# Revit family: Холодильные шкафы со стеклянными дверьми POLAIR Grande
name_source: partatom
category: Оборудование
units: mm (PartAtom-declared; Revit-internal decimal feet)

## family parameters
Всегда вертикально = Да
Классификация = Нет
На основе рабочей плоскости = Нет
Общий = Нет
При загрузке вырезать с полостями = Нет
Размер круглого соединителя = Использовать диаметр
Тип детали = Нормальный
Точка расчета площади = Нет

## types (2) — shared parameters
Высота = 1960 мм
Диап. рабочих температур = +1....+10
Допустимая нагрузка на полку, кг = 40
Замок = опция
Канапе с подсветкой = LED
Клапан Шредера = +
Кол-во полок = 4
Подсветка = LED вертикальная
Размеры в упаковке, мм = 790х744х2125
Расположение агрегата = верхнее
Система электропитания В/Гц = 230/50
Терморегулятор = эл.  блок
Тип оттайки = автомат. с системой исп. конденсата
Тип охлаждения = динамический
Условия окр. среды (темп./вл-сть,%) = до +32/до 60
Хладагент = R134a
Холодильный шкаф = <По категории>
Ширина = 697 мм
zero-valued in all types: Отметка по умолчанию

## per-type parameters (varying)
| type | Вес брутто, кг | Вес нетто, кг | Габаритные размеры, мм | Глубина | Кол-во бутылок 0,5 л по глубине 1 полки, шт. | Кол-во бутылок 0,5 по ширине 1 полки, шт. | Объем, л. | Потребляемая мощность, Вт, не более | Размер полки, мм | Расход электроэнергии за сутки, кВт/ч | Цена, руб. |
| DM105-G | 125 | 106 | 697х710х1960 | 710 мм |  |  | 500 | 350 | 595*455 | 4 | 70 271 |
| DM107-G | 148 | 124 | 697х945х1960 | 945 мм | 9 | 8 | 700 | 400 | 53*650 | 5.5 | 89 034 |
